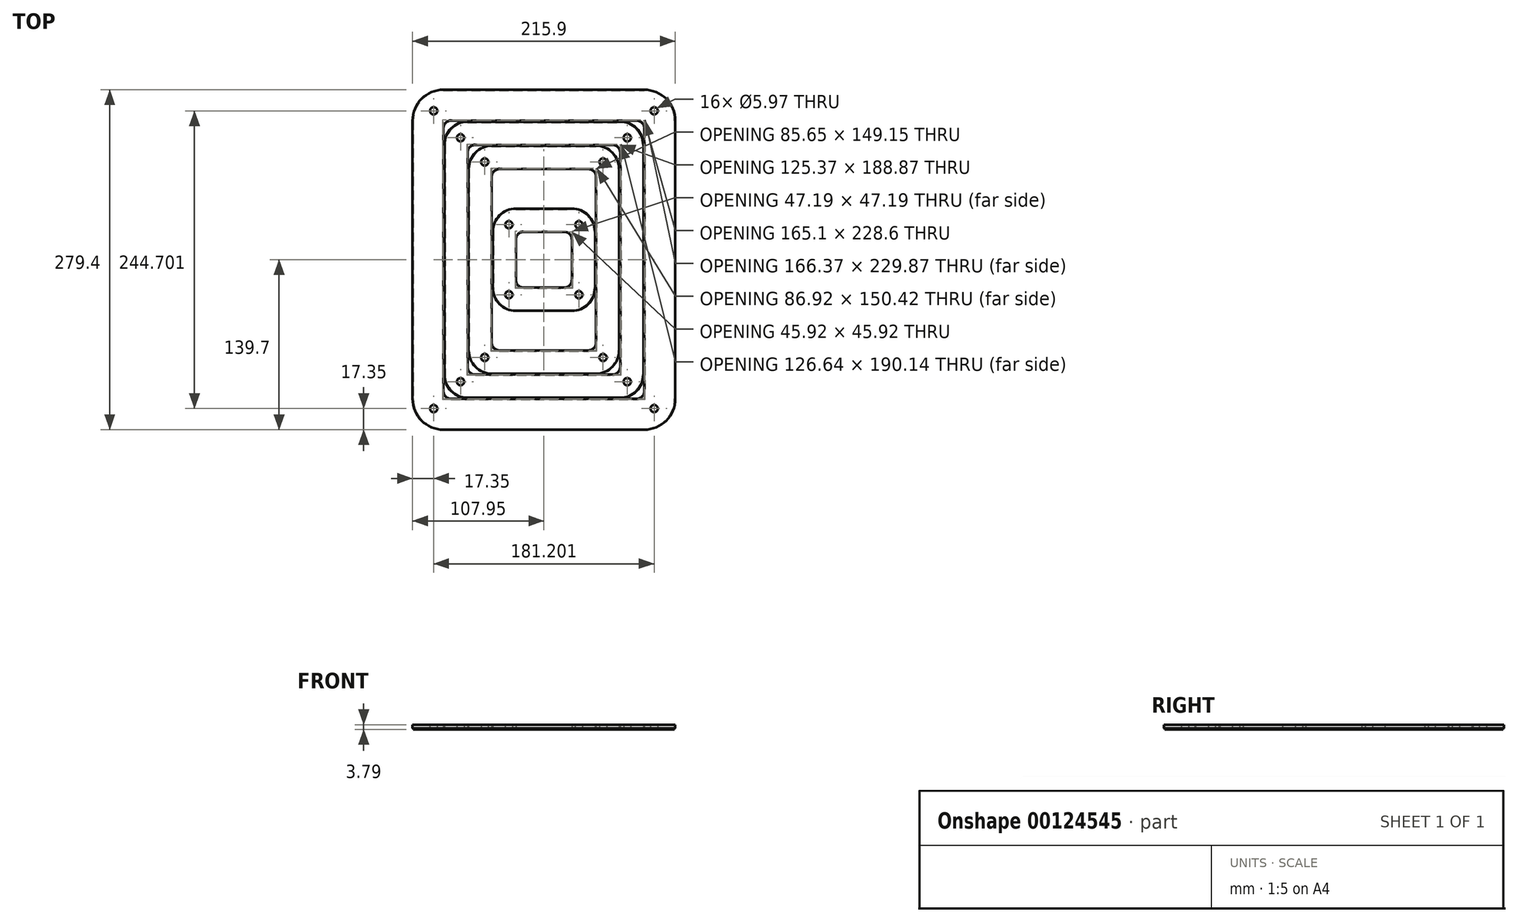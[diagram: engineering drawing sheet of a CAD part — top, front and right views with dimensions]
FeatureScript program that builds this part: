
annotation { "Feature Type Name" : "Feature", "Feature Type Description" : "" }
export const myFeature = defineFeature(function(context is Context, id is Id, definition is map)
    precondition{}
    {
        {
            var Q0;
            Q0=qCreatedBy(makeId("Top.planeOp"),FACE);
            var sketch = newSketch(context, id + "F0", { "sketchPlane" : qUnion([Q0])});
            skLineSegment(sketch, "E0.bottom", {"start": v(-82.55, 139.7) * mm, "end": v(82.55, 139.7) * mm});
            skLineSegment(sketch, "E0.top", {"start": v(-82.55, -139.7) * mm, "end": v(82.55, -139.7) * mm});
            skLineSegment(sketch, "E0.left", {"start": v(-107.95, 114.3) * mm, "end": v(-107.95, -114.3) * mm});
            skLineSegment(sketch, "E0.right", {"start": v(107.95, 114.3) * mm, "end": v(107.95, -114.3) * mm});
            skLineSegment(sketch, "E1.0", {"start": v(-76.2, 114.3) * mm, "end": v(76.2, 114.3) * mm});
            skLineSegment(sketch, "E1.1", {"start": v(-82.55, 107.95) * mm, "end": v(-82.55, -107.95) * mm});
            skLineSegment(sketch, "E1.2", {"start": v(-76.2, -114.3) * mm, "end": v(76.2, -114.3) * mm});
            skLineSegment(sketch, "E1.3", {"start": v(82.55, 107.95) * mm, "end": v(82.55, -107.95) * mm});
            skPoint(sketch, "E2.visualSharp", {"position": v(-82.55, 114.3) * mm});
            skArc(sketch, "E2.filletArc", {"start": v(-76.2, 114.3) * mm, "mid": v(-80.7, 112.44) * mm, "end": v(-82.55, 107.95) * mm});
            skPoint(sketch, "E3.visualSharp", {"position": v(82.55, 114.3) * mm});
            skArc(sketch, "E3.filletArc", {"start": v(82.55, 107.95) * mm, "mid": v(80.7, 112.44) * mm, "end": v(76.2, 114.3) * mm});
            skPoint(sketch, "E4.visualSharp", {"position": v(82.55, -114.3) * mm});
            skArc(sketch, "E4.filletArc", {"start": v(76.2, -114.3) * mm, "mid": v(80.7, -112.44) * mm, "end": v(82.55, -107.95) * mm});
            skPoint(sketch, "E5.visualSharp", {"position": v(-82.55, -114.3) * mm});
            skArc(sketch, "E5.filletArc", {"start": v(-82.55, -107.95) * mm, "mid": v(-80.7, -112.44) * mm, "end": v(-76.2, -114.3) * mm});
            skPoint(sketch, "E6.visualSharp", {"position": v(-107.95, 139.7) * mm});
            skArc(sketch, "E6.filletArc", {"start": v(-82.55, 139.7) * mm, "mid": v(-100.51, 132.26) * mm, "end": v(-107.95, 114.3) * mm});
            skPoint(sketch, "E7.visualSharp", {"position": v(107.95, 139.7) * mm});
            skArc(sketch, "E7.filletArc", {"start": v(107.95, 114.3) * mm, "mid": v(100.51, 132.26) * mm, "end": v(82.55, 139.7) * mm});
            skPoint(sketch, "E8.visualSharp", {"position": v(107.95, -139.7) * mm});
            skArc(sketch, "E8.filletArc", {"start": v(82.55, -139.7) * mm, "mid": v(100.51, -132.26) * mm, "end": v(107.95, -114.3) * mm});
            skPoint(sketch, "E9.visualSharp", {"position": v(-107.95, -139.7) * mm});
            skArc(sketch, "E9.filletArc", {"start": v(-107.95, -114.3) * mm, "mid": v(-100.51, -132.26) * mm, "end": v(-82.55, -139.7) * mm});
            skLineSegment(sketch, "E10", {"start": v(80.7, -112.44) * mm, "end": v(100.51, -132.26) * mm});
            skSolve(sketch);
        }
        {
            var Q0;
            Q0 = qSketchRegion(id + "F0", true);
            extrude(context, id + "F1", {"entities" : qUnion([Q0]), "depth" : 3 * mm});
        }
        {
            var Q0;
            Q0=qCreatedBy(makeId("Top.planeOp"),FACE);
            var sketch = newSketch(context, id + "F2", { "sketchPlane" : qUnion([Q0])});
            skLineSegment(sketch, "E11.bottom", {"start": v(-62.69, 113.49) * mm, "end": v(62.69, 113.49) * mm});
            skLineSegment(sketch, "E11.top", {"start": v(-62.69, -113.49) * mm, "end": v(62.69, -113.49) * mm});
            skLineSegment(sketch, "E11.left", {"start": v(-81.74, 94.44) * mm, "end": v(-81.74, -94.44) * mm});
            skLineSegment(sketch, "E11.right", {"start": v(81.74, 94.44) * mm, "end": v(81.74, -94.44) * mm});
            skLineSegment(sketch, "E12.0", {"start": v(-56.34, 94.44) * mm, "end": v(56.34, 94.44) * mm});
            skLineSegment(sketch, "E12.1", {"start": v(-62.69, 88.09) * mm, "end": v(-62.69, -88.09) * mm});
            skLineSegment(sketch, "E12.2", {"start": v(-56.34, -94.44) * mm, "end": v(56.34, -94.44) * mm});
            skLineSegment(sketch, "E12.3", {"start": v(62.69, 88.09) * mm, "end": v(62.69, -88.09) * mm});
            skPoint(sketch, "E13.visualSharp", {"position": v(-81.74, 113.49) * mm});
            skArc(sketch, "E13.filletArc", {"start": v(-62.69, 113.49) * mm, "mid": v(-76.16, 107.9) * mm, "end": v(-81.74, 94.44) * mm});
            skPoint(sketch, "E14.visualSharp", {"position": v(81.74, 113.49) * mm});
            skArc(sketch, "E14.filletArc", {"start": v(81.74, 94.44) * mm, "mid": v(76.16, 107.9) * mm, "end": v(62.69, 113.49) * mm});
            skPoint(sketch, "E15.visualSharp", {"position": v(81.74, -113.49) * mm});
            skArc(sketch, "E15.filletArc", {"start": v(62.69, -113.49) * mm, "mid": v(76.16, -107.9) * mm, "end": v(81.74, -94.44) * mm});
            skPoint(sketch, "E16.visualSharp", {"position": v(-81.74, -113.49) * mm});
            skArc(sketch, "E16.filletArc", {"start": v(-81.74, -94.44) * mm, "mid": v(-76.16, -107.9) * mm, "end": v(-62.69, -113.49) * mm});
            skArc(sketch, "E17.filletArc", {"start": v(-56.34, 94.44) * mm, "mid": v(-60.83, 92.58) * mm, "end": v(-62.69, 88.09) * mm});
            skArc(sketch, "E18.filletArc", {"start": v(62.69, 88.09) * mm, "mid": v(60.83, 92.58) * mm, "end": v(56.34, 94.44) * mm});
            skArc(sketch, "E19.filletArc", {"start": v(56.34, -94.44) * mm, "mid": v(60.83, -92.58) * mm, "end": v(62.69, -88.09) * mm});
            skArc(sketch, "E20.filletArc", {"start": v(-62.69, -88.09) * mm, "mid": v(-60.83, -92.58) * mm, "end": v(-56.34, -94.44) * mm});
            skSolve(sketch);
        }
        {
            var Q0;
            Q0 = qSketchRegion(id + "F2", true);
            var Q1;
            Q1=makeQuery(id+"F1.opExtrude","CAP_FACE",FACE,{"disambiguationData":[OSD([sQuery(id+"F0.wireOp",EDGE,"E0.bottom"),sQuery(id+"F0.wireOp",EDGE,"E0.top"),sQuery(id+"F0.wireOp",EDGE,"E0.left"),sQuery(id+"F0.wireOp",EDGE,"E0.right"),sQuery(id+"F0.wireOp",EDGE,"E1.0"),sQuery(id+"F0.wireOp",EDGE,"E1.1"),sQuery(id+"F0.wireOp",EDGE,"E1.2"),sQuery(id+"F0.wireOp",EDGE,"E1.3"),sQuery(id+"F0.wireOp",EDGE,"E2.filletArc"),sQuery(id+"F0.wireOp",EDGE,"E3.filletArc"),sQuery(id+"F0.wireOp",EDGE,"E4.filletArc"),sQuery(id+"F0.wireOp",EDGE,"E5.filletArc"),sQuery(id+"F0.wireOp",EDGE,"E6.filletArc"),sQuery(id+"F0.wireOp",EDGE,"E7.filletArc"),sQuery(id+"F0.wireOp",EDGE,"E8.filletArc"),sQuery(id+"F0.wireOp",EDGE,"E9.filletArc")])],"isStart":false});
            extrude(context, id + "F3", {"entities" : qUnion([Q0]), "endBound" : BoundingType.UP_TO_SURFACE, "endBoundEntityFace" : qUnion([Q1]), "depth" : 3.17 * mm});
        }
        {
            var Q0;
            Q0=qCreatedBy(makeId("Top.planeOp"),FACE);
            var sketch = newSketch(context, id + "F4", { "sketchPlane" : qUnion([Q0])});
            skLineSegment(sketch, "E21.bottom", {"start": v(-42.82, 93.62) * mm, "end": v(42.82, 93.62) * mm});
            skLineSegment(sketch, "E21.top", {"start": v(-42.82, -93.62) * mm, "end": v(42.82, -93.62) * mm});
            skLineSegment(sketch, "E21.left", {"start": v(-61.87, 74.57) * mm, "end": v(-61.87, -74.57) * mm});
            skLineSegment(sketch, "E21.right", {"start": v(61.87, 74.57) * mm, "end": v(61.87, -74.57) * mm});
            skLineSegment(sketch, "E22.0", {"start": v(-36.47, 74.57) * mm, "end": v(36.47, 74.57) * mm});
            skLineSegment(sketch, "E22.1", {"start": v(-42.82, 68.22) * mm, "end": v(-42.82, -68.22) * mm});
            skLineSegment(sketch, "E22.2", {"start": v(-36.47, -74.57) * mm, "end": v(36.47, -74.57) * mm});
            skLineSegment(sketch, "E22.3", {"start": v(42.82, 68.22) * mm, "end": v(42.82, -68.22) * mm});
            skPoint(sketch, "E23.visualSharp", {"position": v(-61.87, 93.62) * mm});
            skArc(sketch, "E23.filletArc", {"start": v(-42.82, 93.62) * mm, "mid": v(-56.3, 88.04) * mm, "end": v(-61.87, 74.57) * mm});
            skPoint(sketch, "E24.visualSharp", {"position": v(61.87, 93.62) * mm});
            skArc(sketch, "E24.filletArc", {"start": v(61.87, 74.57) * mm, "mid": v(56.3, 88.04) * mm, "end": v(42.82, 93.62) * mm});
            skPoint(sketch, "E25.visualSharp", {"position": v(61.87, -93.62) * mm});
            skArc(sketch, "E25.filletArc", {"start": v(42.82, -93.62) * mm, "mid": v(56.3, -88.04) * mm, "end": v(61.87, -74.57) * mm});
            skPoint(sketch, "E26.visualSharp", {"position": v(-61.87, -93.62) * mm});
            skArc(sketch, "E26.filletArc", {"start": v(-61.87, -74.57) * mm, "mid": v(-56.3, -88.04) * mm, "end": v(-42.82, -93.62) * mm});
            skArc(sketch, "E27.filletArc", {"start": v(-36.47, 74.57) * mm, "mid": v(-40.96, 72.71) * mm, "end": v(-42.82, 68.22) * mm});
            skArc(sketch, "E28.filletArc", {"start": v(42.82, 68.22) * mm, "mid": v(40.96, 72.71) * mm, "end": v(36.47, 74.57) * mm});
            skArc(sketch, "E29.filletArc", {"start": v(36.47, -74.57) * mm, "mid": v(40.96, -72.71) * mm, "end": v(42.82, -68.22) * mm});
            skArc(sketch, "E30.filletArc", {"start": v(-42.82, -68.22) * mm, "mid": v(-40.96, -72.71) * mm, "end": v(-36.47, -74.57) * mm});
            skSolve(sketch);
        }
        {
            var Q0;
            Q0 = qSketchRegion(id + "F4", true);
            var Q1;
            Q1=makeQuery(id+"F1.opExtrude","CAP_FACE",FACE,{"disambiguationData":[OSD([sQuery(id+"F0.wireOp",EDGE,"E0.bottom"),sQuery(id+"F0.wireOp",EDGE,"E0.top"),sQuery(id+"F0.wireOp",EDGE,"E0.left"),sQuery(id+"F0.wireOp",EDGE,"E0.right"),sQuery(id+"F0.wireOp",EDGE,"E1.0"),sQuery(id+"F0.wireOp",EDGE,"E1.1"),sQuery(id+"F0.wireOp",EDGE,"E1.2"),sQuery(id+"F0.wireOp",EDGE,"E1.3"),sQuery(id+"F0.wireOp",EDGE,"E2.filletArc"),sQuery(id+"F0.wireOp",EDGE,"E3.filletArc"),sQuery(id+"F0.wireOp",EDGE,"E4.filletArc"),sQuery(id+"F0.wireOp",EDGE,"E5.filletArc"),sQuery(id+"F0.wireOp",EDGE,"E6.filletArc"),sQuery(id+"F0.wireOp",EDGE,"E7.filletArc"),sQuery(id+"F0.wireOp",EDGE,"E8.filletArc"),sQuery(id+"F0.wireOp",EDGE,"E9.filletArc")])],"isStart":false});
            extrude(context, id + "F5", {"entities" : qUnion([Q0]), "endBound" : BoundingType.UP_TO_SURFACE, "endBoundEntityFace" : qUnion([Q1]), "depth" : 3.17 * mm});
        }
        {
            var Q0;
            Q0=qCreatedBy(makeId("Top.planeOp"),FACE);
            var sketch = newSketch(context, id + "F6", { "sketchPlane" : qUnion([Q0])});
            skLineSegment(sketch, "E31.bottom", {"start": v(-22.96, 42.01) * mm, "end": v(22.96, 42.01) * mm});
            skLineSegment(sketch, "E31.top", {"start": v(-22.96, -42.01) * mm, "end": v(22.96, -42.01) * mm});
            skLineSegment(sketch, "E31.left", {"start": v(-42.01, 22.96) * mm, "end": v(-42.01, -22.96) * mm});
            skLineSegment(sketch, "E31.right", {"start": v(42.01, 22.96) * mm, "end": v(42.01, -22.96) * mm});
            skLineSegment(sketch, "E32.0", {"start": v(-16.61, 22.96) * mm, "end": v(16.61, 22.96) * mm});
            skLineSegment(sketch, "E32.1", {"start": v(-22.96, 16.61) * mm, "end": v(-22.96, -16.61) * mm});
            skLineSegment(sketch, "E32.2", {"start": v(-16.61, -22.96) * mm, "end": v(16.61, -22.96) * mm});
            skLineSegment(sketch, "E32.3", {"start": v(22.96, 16.61) * mm, "end": v(22.96, -16.61) * mm});
            skPoint(sketch, "E33.visualSharp", {"position": v(-42.01, 42.01) * mm});
            skArc(sketch, "E33.filletArc", {"start": v(-22.96, 42.01) * mm, "mid": v(-36.43, 36.43) * mm, "end": v(-42.01, 22.96) * mm});
            skPoint(sketch, "E34.visualSharp", {"position": v(42.01, 42.01) * mm});
            skArc(sketch, "E34.filletArc", {"start": v(42.01, 22.96) * mm, "mid": v(36.43, 36.43) * mm, "end": v(22.96, 42.01) * mm});
            skPoint(sketch, "E35.visualSharp", {"position": v(42.01, -42.01) * mm});
            skArc(sketch, "E35.filletArc", {"start": v(22.96, -42.01) * mm, "mid": v(36.43, -36.43) * mm, "end": v(42.01, -22.96) * mm});
            skPoint(sketch, "E36.visualSharp", {"position": v(-42.01, -42.01) * mm});
            skArc(sketch, "E36.filletArc", {"start": v(-42.01, -22.96) * mm, "mid": v(-36.43, -36.43) * mm, "end": v(-22.96, -42.01) * mm});
            skArc(sketch, "E37.filletArc", {"start": v(22.96, 16.61) * mm, "mid": v(21.1, 21.1) * mm, "end": v(16.61, 22.96) * mm});
            skArc(sketch, "E38.filletArc", {"start": v(16.61, -22.96) * mm, "mid": v(21.1, -21.1) * mm, "end": v(22.96, -16.61) * mm});
            skArc(sketch, "E39.filletArc", {"start": v(-22.96, -16.61) * mm, "mid": v(-21.1, -21.1) * mm, "end": v(-16.61, -22.96) * mm});
            skArc(sketch, "E40.filletArc", {"start": v(-16.61, 22.96) * mm, "mid": v(-21.1, 21.1) * mm, "end": v(-22.96, 16.61) * mm});
            skSolve(sketch);
        }
        {
            var Q0;
            Q0=makeQuery(id+"F6.imprint","IMPRINT",FACE,{"disambiguationData":[TD([[makeQuery(id+"F6.imprint","IMPRINT",EDGE,{"derivedFrom":sQuery(id+"F6.wireOp",EDGE,"E31.bottom")}),-1.0]])]});
            var Q1;
            Q1=makeQuery(id+"F1.opExtrude","CAP_FACE",FACE,{"disambiguationData":[OSD([sQuery(id+"F0.wireOp",EDGE,"E0.bottom"),sQuery(id+"F0.wireOp",EDGE,"E0.top"),sQuery(id+"F0.wireOp",EDGE,"E0.left"),sQuery(id+"F0.wireOp",EDGE,"E0.right"),sQuery(id+"F0.wireOp",EDGE,"E1.0"),sQuery(id+"F0.wireOp",EDGE,"E1.1"),sQuery(id+"F0.wireOp",EDGE,"E1.2"),sQuery(id+"F0.wireOp",EDGE,"E1.3"),sQuery(id+"F0.wireOp",EDGE,"E2.filletArc"),sQuery(id+"F0.wireOp",EDGE,"E3.filletArc"),sQuery(id+"F0.wireOp",EDGE,"E4.filletArc"),sQuery(id+"F0.wireOp",EDGE,"E5.filletArc"),sQuery(id+"F0.wireOp",EDGE,"E6.filletArc"),sQuery(id+"F0.wireOp",EDGE,"E7.filletArc"),sQuery(id+"F0.wireOp",EDGE,"E8.filletArc"),sQuery(id+"F0.wireOp",EDGE,"E9.filletArc")])],"isStart":false});
            extrude(context, id + "F7", {"entities" : qUnion([Q0]), "endBound" : BoundingType.UP_TO_SURFACE, "endBoundEntityFace" : qUnion([Q1]), "depth" : 3.17 * mm});
        }
        {
            var Q0;
            Q0=qCreatedBy(makeId("Top.planeOp"),FACE);
            var sketch = newSketch(context, id + "F8", { "sketchPlane" : qUnion([Q0])});
            skLineSegment(sketch, "E41", {"start": v(-80.7, 112.44) * mm, "end": v(-100.51, 132.26) * mm});
            skLineSegment(sketch, "E42", {"start": v(-76.16, 107.9) * mm, "end": v(-60.83, 92.58) * mm});
            skLineSegment(sketch, "E43", {"start": v(-56.3, 88.04) * mm, "end": v(-40.96, 72.71) * mm});
            skLineSegment(sketch, "E44", {"start": v(-36.43, 36.43) * mm, "end": v(-21.1, 21.1) * mm});
            skCircle(sketch, "E45", {"center": v(-90.6, 122.35) * mm, "radius": 2.98 * mm});
            skCircle(sketch, "E46", {"center": v(-68.5, 100.24) * mm, "radius": 2.98 * mm});
            skCircle(sketch, "E47", {"center": v(-48.63, 80.38) * mm, "radius": 2.98 * mm});
            skCircle(sketch, "E48", {"center": v(-28.77, 28.77) * mm, "radius": 2.98 * mm});
            skCircle(sketch, "E49.MirrorC", {"center": v(-28.77, -28.77) * mm, "radius": 2.98 * mm});
            skCircle(sketch, "E50.MirrorC", {"center": v(-48.63, -80.38) * mm, "radius": 2.98 * mm});
            skCircle(sketch, "E51.MirrorC", {"center": v(-68.5, -100.24) * mm, "radius": 2.98 * mm});
            skCircle(sketch, "E52.MirrorC", {"center": v(-90.6, -122.35) * mm, "radius": 2.98 * mm});
            skCircle(sketch, "E53.MirrorC", {"center": v(90.6, 122.35) * mm, "radius": 2.98 * mm});
            skCircle(sketch, "E54.MirrorC", {"center": v(68.5, 100.24) * mm, "radius": 2.98 * mm});
            skCircle(sketch, "E55.MirrorC", {"center": v(48.63, 80.38) * mm, "radius": 2.98 * mm});
            skCircle(sketch, "E56.MirrorC", {"center": v(28.77, 28.77) * mm, "radius": 2.98 * mm});
            skCircle(sketch, "E57.MirrorC", {"center": v(28.77, -28.77) * mm, "radius": 2.98 * mm});
            skCircle(sketch, "E58.MirrorC", {"center": v(48.63, -80.38) * mm, "radius": 2.98 * mm});
            skCircle(sketch, "E59.MirrorC", {"center": v(68.5, -100.24) * mm, "radius": 2.98 * mm});
            skCircle(sketch, "E60.MirrorC", {"center": v(90.6, -122.35) * mm, "radius": 2.98 * mm});
            skSolve(sketch);
        }
        {
            var Q0;
            Q0 = qSketchRegion(id + "F8", true);
            extrude(context, id + "F9", {"entities" : qUnion([Q0]), "operationType" : NewBodyOperationType.REMOVE, "endBound" : BoundingType.THROUGH_ALL, "depth" : 25.4 * mm});
        }
        {
            var Q0;
            Q0=qCreatedBy(makeId("Top.planeOp"),FACE);
            var sketch = newSketch(context, id + "F10", { "sketchPlane" : qUnion([Q0])});
            skLineSegment(sketch, "E61.0", {"start": v(107.32, 114.3) * mm, "end": v(107.31, -114.3) * mm});
            skArc(sketch, "E61.1", {"start": v(82.55, -139.06) * mm, "mid": v(100.06, -131.81) * mm, "end": v(107.31, -114.3) * mm});
            skArc(sketch, "E61.2", {"start": v(107.31, 114.3) * mm, "mid": v(100.06, 131.81) * mm, "end": v(82.55, 139.07) * mm});
            skLineSegment(sketch, "E61.3", {"start": v(-82.55, -139.07) * mm, "end": v(82.55, -139.07) * mm});
            skLineSegment(sketch, "E61.4", {"start": v(-82.55, 139.07) * mm, "end": v(82.55, 139.06) * mm});
            skArc(sketch, "E61.5", {"start": v(-82.55, 139.06) * mm, "mid": v(-100.06, 131.81) * mm, "end": v(-107.31, 114.3) * mm});
            skLineSegment(sketch, "E61.6", {"start": v(-107.31, 114.3) * mm, "end": v(-107.32, -114.3) * mm});
            skArc(sketch, "E61.7", {"start": v(-107.31, -114.3) * mm, "mid": v(-100.06, -131.81) * mm, "end": v(-82.55, -139.06) * mm});
            skLineSegment(sketch, "E62.0", {"start": v(83.19, 107.95) * mm, "end": v(83.18, -107.95) * mm});
            skArc(sketch, "E62.1", {"start": v(76.2, -114.94) * mm, "mid": v(81.14, -112.89) * mm, "end": v(83.18, -107.95) * mm});
            skArc(sketch, "E62.2", {"start": v(83.19, 107.95) * mm, "mid": v(81.14, 112.89) * mm, "end": v(76.2, 114.94) * mm});
            skLineSegment(sketch, "E62.3", {"start": v(-76.2, -114.93) * mm, "end": v(76.2, -114.94) * mm});
            skLineSegment(sketch, "E62.4", {"start": v(-76.2, 114.94) * mm, "end": v(76.2, 114.93) * mm});
            skArc(sketch, "E62.5", {"start": v(-76.2, 114.94) * mm, "mid": v(-81.14, 112.89) * mm, "end": v(-83.18, 107.95) * mm});
            skLineSegment(sketch, "E62.6", {"start": v(-83.18, 107.95) * mm, "end": v(-83.19, -107.95) * mm});
            skArc(sketch, "E62.7", {"start": v(-83.19, -107.95) * mm, "mid": v(-81.14, -112.89) * mm, "end": v(-76.2, -114.93) * mm});
            skSolve(sketch);
        }
        {
            var Q0;
            Q0 = qSketchRegion(id + "F10", true);
            extrude(context, id + "F11", {"entities" : qUnion([Q0]), "oppositeDirection" : true, "depth" : 0.8 * mm});
        }
        {
            var Q0;
            Q0=qCreatedBy(makeId("Top.planeOp"),FACE);
            var sketch = newSketch(context, id + "F12", { "sketchPlane" : qUnion([Q0])});
            skLineSegment(sketch, "E63.0", {"start": v(81.1, 94.44) * mm, "end": v(81.1, -94.44) * mm});
            skArc(sketch, "E63.1", {"start": v(62.69, -112.85) * mm, "mid": v(75.7, -107.46) * mm, "end": v(81.1, -94.44) * mm});
            skArc(sketch, "E63.2", {"start": v(81.1, 94.44) * mm, "mid": v(75.7, 107.46) * mm, "end": v(62.69, 112.85) * mm});
            skLineSegment(sketch, "E63.3", {"start": v(-62.69, -112.85) * mm, "end": v(62.69, -112.85) * mm});
            skLineSegment(sketch, "E63.4", {"start": v(-62.69, 112.85) * mm, "end": v(62.69, 112.85) * mm});
            skArc(sketch, "E63.5", {"start": v(-62.69, 112.85) * mm, "mid": v(-75.7, 107.46) * mm, "end": v(-81.1, 94.44) * mm});
            skLineSegment(sketch, "E63.6", {"start": v(-81.1, 94.44) * mm, "end": v(-81.1, -94.44) * mm});
            skArc(sketch, "E63.7", {"start": v(-81.1, -94.44) * mm, "mid": v(-75.7, -107.46) * mm, "end": v(-62.69, -112.85) * mm});
            skLineSegment(sketch, "E64.0", {"start": v(63.32, 88.09) * mm, "end": v(63.32, -88.09) * mm});
            skArc(sketch, "E64.1", {"start": v(56.34, -95.07) * mm, "mid": v(61.28, -93.03) * mm, "end": v(63.32, -88.09) * mm});
            skArc(sketch, "E64.2", {"start": v(63.32, 88.09) * mm, "mid": v(61.28, 93.03) * mm, "end": v(56.34, 95.07) * mm});
            skLineSegment(sketch, "E64.3", {"start": v(-56.34, -95.07) * mm, "end": v(56.34, -95.07) * mm});
            skLineSegment(sketch, "E64.4", {"start": v(-56.34, 95.07) * mm, "end": v(56.34, 95.07) * mm});
            skArc(sketch, "E64.5", {"start": v(-56.34, 95.07) * mm, "mid": v(-61.28, 93.03) * mm, "end": v(-63.32, 88.09) * mm});
            skLineSegment(sketch, "E64.6", {"start": v(-63.32, 88.09) * mm, "end": v(-63.32, -88.09) * mm});
            skArc(sketch, "E64.7", {"start": v(-63.32, -88.09) * mm, "mid": v(-61.28, -93.03) * mm, "end": v(-56.34, -95.07) * mm});
            skSolve(sketch);
        }
        {
            var Q0;
            Q0 = qSketchRegion(id + "F12", true);
            extrude(context, id + "F13", {"entities" : qUnion([Q0]), "oppositeDirection" : true, "depth" : 0.8 * mm});
        }
        {
            var Q0;
            Q0=qCreatedBy(makeId("Top.planeOp"),FACE);
            var sketch = newSketch(context, id + "F14", { "sketchPlane" : qUnion([Q0])});
            skLineSegment(sketch, "E65.0", {"start": v(61.24, 74.57) * mm, "end": v(61.24, -74.57) * mm});
            skArc(sketch, "E65.1", {"start": v(42.82, -92.99) * mm, "mid": v(55.85, -87.6) * mm, "end": v(61.24, -74.57) * mm});
            skArc(sketch, "E65.2", {"start": v(61.24, 74.57) * mm, "mid": v(55.85, 87.6) * mm, "end": v(42.82, 92.99) * mm});
            skLineSegment(sketch, "E65.3", {"start": v(-42.82, -92.99) * mm, "end": v(42.82, -92.99) * mm});
            skLineSegment(sketch, "E65.4", {"start": v(-42.82, 92.99) * mm, "end": v(42.82, 92.99) * mm});
            skArc(sketch, "E65.5", {"start": v(-42.82, 92.99) * mm, "mid": v(-55.85, 87.6) * mm, "end": v(-61.24, 74.57) * mm});
            skLineSegment(sketch, "E65.6", {"start": v(-61.24, 74.57) * mm, "end": v(-61.24, -74.57) * mm});
            skArc(sketch, "E65.7", {"start": v(-61.24, -74.57) * mm, "mid": v(-55.85, -87.6) * mm, "end": v(-42.82, -92.99) * mm});
            skLineSegment(sketch, "E66.0", {"start": v(43.46, 68.22) * mm, "end": v(43.46, -68.22) * mm});
            skArc(sketch, "E66.1", {"start": v(36.47, -75.2) * mm, "mid": v(41.41, -73.16) * mm, "end": v(43.46, -68.22) * mm});
            skArc(sketch, "E66.2", {"start": v(43.46, 68.22) * mm, "mid": v(41.41, 73.16) * mm, "end": v(36.47, 75.2) * mm});
            skLineSegment(sketch, "E66.3", {"start": v(-36.47, -75.2) * mm, "end": v(36.47, -75.2) * mm});
            skLineSegment(sketch, "E66.4", {"start": v(-36.47, 75.2) * mm, "end": v(36.47, 75.2) * mm});
            skArc(sketch, "E66.5", {"start": v(-36.47, 75.2) * mm, "mid": v(-41.41, 73.16) * mm, "end": v(-43.46, 68.22) * mm});
            skLineSegment(sketch, "E66.6", {"start": v(-43.46, 68.22) * mm, "end": v(-43.46, -68.22) * mm});
            skArc(sketch, "E66.7", {"start": v(-43.46, -68.22) * mm, "mid": v(-41.41, -73.16) * mm, "end": v(-36.47, -75.2) * mm});
            skSolve(sketch);
        }
        {
            var Q0;
            Q0 = qSketchRegion(id + "F14", true);
            extrude(context, id + "F15", {"entities" : qUnion([Q0]), "oppositeDirection" : true, "depth" : 0.8 * mm});
        }
        {
            var Q0;
            Q0=qCreatedBy(makeId("Top.planeOp"),FACE);
            var sketch = newSketch(context, id + "F16", { "sketchPlane" : qUnion([Q0])});
            skLineSegment(sketch, "E67.0", {"start": v(41.38, 22.96) * mm, "end": v(41.38, -22.96) * mm});
            skArc(sketch, "E67.1", {"start": v(22.96, -41.38) * mm, "mid": v(35.98, -35.98) * mm, "end": v(41.38, -22.96) * mm});
            skArc(sketch, "E67.2", {"start": v(41.38, 22.96) * mm, "mid": v(35.98, 35.98) * mm, "end": v(22.96, 41.38) * mm});
            skLineSegment(sketch, "E67.3", {"start": v(-22.96, -41.38) * mm, "end": v(22.96, -41.38) * mm});
            skLineSegment(sketch, "E67.4", {"start": v(-22.96, 41.38) * mm, "end": v(22.96, 41.38) * mm});
            skArc(sketch, "E67.5", {"start": v(-22.96, 41.38) * mm, "mid": v(-35.98, 35.98) * mm, "end": v(-41.38, 22.96) * mm});
            skLineSegment(sketch, "E67.6", {"start": v(-41.38, 22.96) * mm, "end": v(-41.38, -22.96) * mm});
            skArc(sketch, "E67.7", {"start": v(-41.38, -22.96) * mm, "mid": v(-35.98, -35.98) * mm, "end": v(-22.96, -41.38) * mm});
            skLineSegment(sketch, "E68.0", {"start": v(23.6, 16.61) * mm, "end": v(23.6, -16.61) * mm});
            skArc(sketch, "E68.1", {"start": v(16.61, -23.6) * mm, "mid": v(21.55, -21.55) * mm, "end": v(23.6, -16.61) * mm});
            skArc(sketch, "E68.2", {"start": v(23.6, 16.61) * mm, "mid": v(21.55, 21.55) * mm, "end": v(16.61, 23.6) * mm});
            skLineSegment(sketch, "E68.3", {"start": v(-16.61, -23.6) * mm, "end": v(16.61, -23.6) * mm});
            skLineSegment(sketch, "E68.4", {"start": v(-16.61, 23.6) * mm, "end": v(16.61, 23.6) * mm});
            skArc(sketch, "E68.5", {"start": v(-16.61, 23.6) * mm, "mid": v(-21.55, 21.55) * mm, "end": v(-23.6, 16.61) * mm});
            skLineSegment(sketch, "E68.6", {"start": v(-23.6, 16.61) * mm, "end": v(-23.6, -16.61) * mm});
            skArc(sketch, "E68.7", {"start": v(-23.6, -16.61) * mm, "mid": v(-21.55, -21.55) * mm, "end": v(-16.61, -23.6) * mm});
            skSolve(sketch);
        }
        {
            var Q0;
            Q0 = qSketchRegion(id + "F16", true);
            extrude(context, id + "F17", {"entities" : qUnion([Q0]), "oppositeDirection" : true, "depth" : 0.8 * mm});
        }
    });
